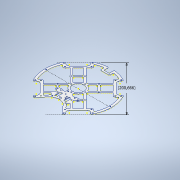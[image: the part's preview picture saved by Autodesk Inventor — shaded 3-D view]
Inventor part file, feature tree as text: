
AUTODESK INVENTOR PART (.ipt)
format: ipt  version: 2020 (Build 240168000, 168)  size: 2,100,224 bytes
history: native  units: mm
features: extrude x15, sketch x12, projected_geometry x11, fillet x2, other x1, chamfer x1
ambient origin geometry x8: Origin, YZ Plane, XZ Plane, XY Plane, X Axis, Y Axis, Z Axis, Center Point
bodies: Body1 (feature_tree)
feature tree (42):
  other  "Твердое тело1"
  extrude  "outer"  TaperAngle=45.0deg  [1 undecoded]
  extrude  "inner"  Depth=7.0mm
  sketch  "Эскиз3"
  extrude  "Выдавливание3"  Depth=20.0mm
  extrude  "Выдавливание4"  Depth=7.0mm
  extrude  "Выдавливание5"  Depth=3.2mm
  sketch  "Эскиз5"
  extrude  "Выдавливание7"  Depth=59.0mm
  extrude  "Выдавливание8"  Depth=83.0mm
  sketch  "Эскиз6"
  extrude  "Выдавливание9"  Depth=69.0mm
  extrude  "Выдавливание10"  Depth=55.0mm
  sketch  "Эскиз7"
  sketch  "Эскиз8"
  sketch  "Эскиз9"
  extrude  "Выдавливание11"  Depth=3.0mm
  extrude  "Выдавливание12"  Depth=8.0mm
  sketch  "Эскиз10"
  extrude  "Выдавливание13"  Depth=5.0mm
  extrude  "Выдавливание14"  Depth=2.0mm
  fillet  "Сопряжение1"  Radius=40.0mm
  chamfer  "Фаска1"  Distance=2.0mm
  sketch  "Эскиз11"
  extrude  "Выдавливание15"  Depth=105.0mm
  fillet  "Сопряжение2"  Radius=2.0mm
  extrude  "Выдавливание16"  Depth=2.0mm TaperAngle=0.0deg
  sketch  "Эскиз1"
  sketch  "Эскиз2"
  projected_geometry  "Спроецированная петля1"
  projected_geometry  "Спроецированная петля2"
  sketch  "Эскиз4"
  projected_geometry  "Спроецированная петля3"
  projected_geometry  "Спроецированная петля4"
  projected_geometry  "Спроецированная петля5"
  projected_geometry  "Спроецированная петля6"
  projected_geometry  "Спроецированная петля7"
  projected_geometry  "Спроецированная петля8"
  projected_geometry  "Спроецированная петля9"
  sketch  "Эскиз12"
  projected_geometry  "Спроецированная петля10"
  projected_geometry  "Спроецированная петля11"
note: 1 required parameter value undecoded (feature->parameter linkage not recoverable at this tier; creation-order binding heuristic only, values carry confidence <= 0.55)
